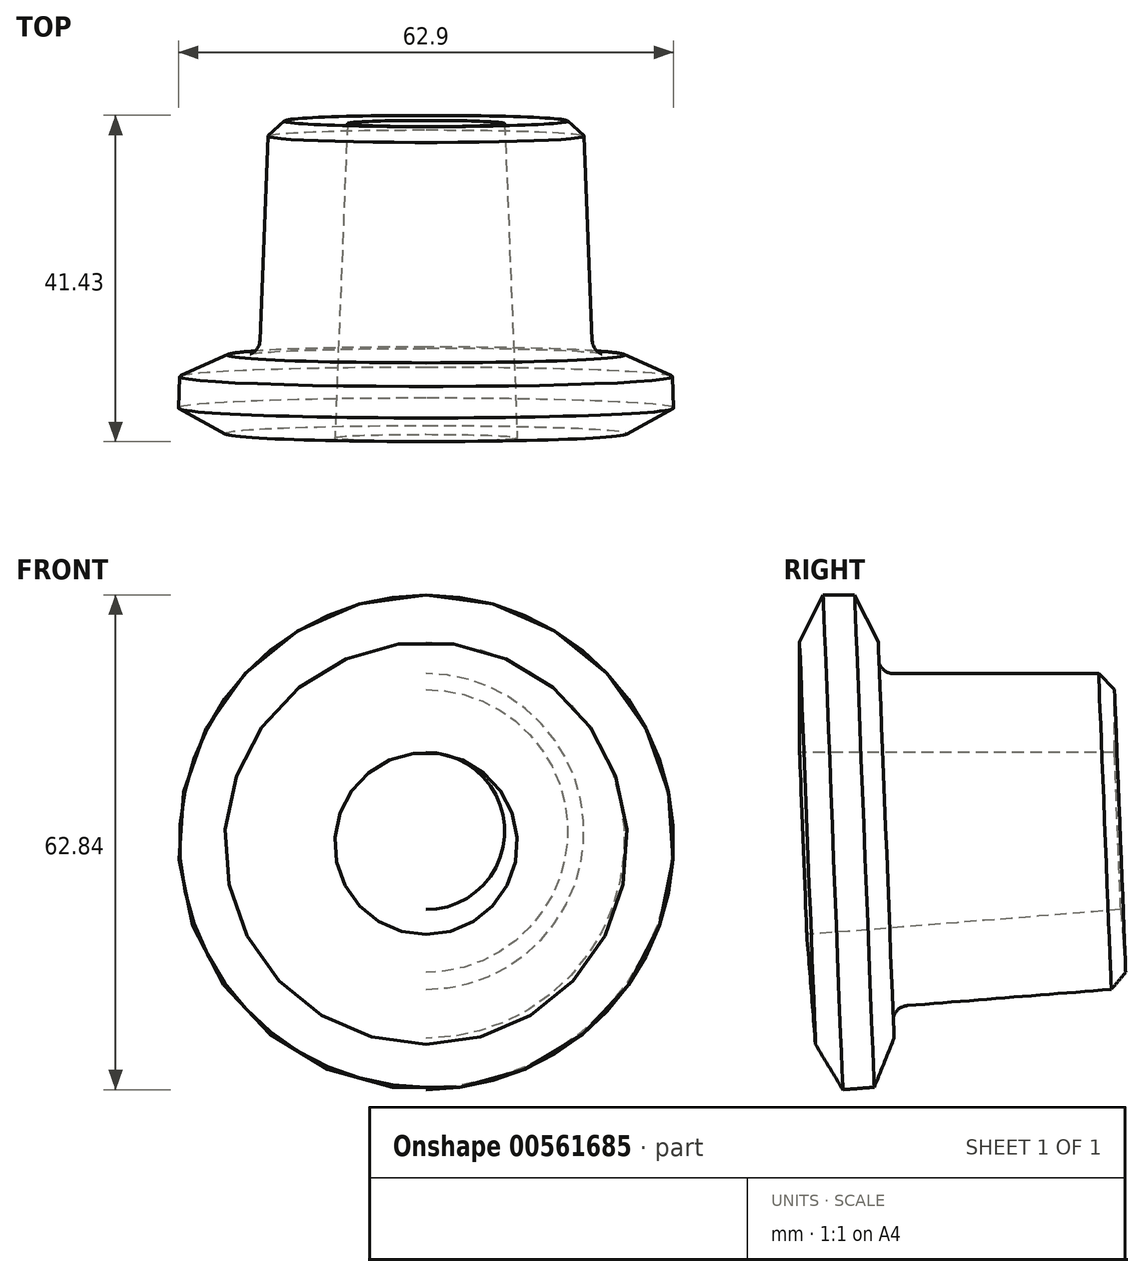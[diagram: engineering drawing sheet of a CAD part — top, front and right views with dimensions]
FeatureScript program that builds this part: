
annotation { "Feature Type Name" : "Feature", "Feature Type Description" : "" }
export const myFeature = defineFeature(function(context is Context, id is Id, definition is map)
    precondition{}
    {
        {
            var Q0;
            Q0=qCreatedBy(makeId("Right.planeOp"),FACE);
            var sketch = newSketch(context, id + "F0", { "sketchPlane" : qUnion([Q0])});
            skLineSegment(sketch, "E0.top", {"start": v(27.86, 32.7) * mm, "end": v(37.86, 32.7) * mm});
            skLineSegment(sketch, "E1.top", {"start": v(27.86, 22.7) * mm, "end": v(67.86, 22.7) * mm});
            skLineSegment(sketch, "E1.right", {"start": v(67.86, 12.7) * mm, "end": v(67.86, 22.7) * mm});
            skLineSegment(sketch, "E2.MirrorCS", {"start": v(27.86, 12.7) * mm, "end": v(31.57, 12.7) * mm});
            skLineSegment(sketch, "E3.MirrorCS", {"start": v(37.86, 12.7) * mm, "end": v(67.86, 12.7) * mm});
            skLineSegment(sketch, "E4", {"start": v(31.57, 12.7) * mm, "end": v(37.86, 12.7) * mm});
            skLineSegment(sketch, "E5", {"start": v(27.86, 12.7) * mm, "end": v(27.86, 22.7) * mm});
            skLineSegment(sketch, "E6", {"start": v(37.86, 12.7) * mm, "end": v(37.86, 32.7) * mm});
            skLineSegment(sketch, "E7.trimOffspring", {"start": v(27.86, 12.7) * mm, "end": v(27.86, 32.7) * mm});
            skLineSegment(sketch, "E8", {"start": v(27.86, 12.7) * mm, "end": v(27.86, -7.3) * mm, "construction": true});
            skLineSegment(sketch, "E9", {"start": v(37.86, 12.7) * mm, "end": v(37.86, -7.3) * mm, "construction": true});
            skLineSegment(sketch, "E10", {"start": v(67.86, 12.7) * mm, "end": v(67.86, -7.3) * mm, "construction": true});
            skLineSegment(sketch, "E11", {"start": v(0, 0) * mm, "end": v(67.86, 2.7) * mm, "construction": true});
            skSolve(sketch);
        }
        {
            var Q0;
            {var subQ6=sQuery(id+"F0.wireOp",EDGE,"E2.MirrorCS");Q0=makeQuery(id+"F0.imprint","IMPRINT",FACE,{"disambiguationData":[TD([[makeQuery(id+"F0.imprint","IMPRINT",EDGE,{"derivedFrom":subQ6}),1.0]])]});}
            var Q1;
            {var subQ0=sQuery(id+"F0.wireOp",EDGE,"E1.right");Q1=makeQuery(id+"F0.imprint","IMPRINT",FACE,{"disambiguationData":[TD([[makeQuery(id+"F0.imprint","IMPRINT",EDGE,{"derivedFrom":subQ0}),1.0]])]});}
            var Q2;
            {var subQ0=sQuery(id+"F0.wireOp",EDGE,"E0.top");Q2=makeQuery(id+"F0.imprint","IMPRINT",FACE,{"disambiguationData":[TD([[makeQuery(id+"F0.imprint","IMPRINT",EDGE,{"derivedFrom":subQ0}),-1.0]])]});}
            var Q3;
            Q3=sQuery(id+"F0.wireOp",EDGE,"E11");
            revolve(context, id + "F1", {"entities" : qUnion([Q0, Q1, Q2]), "axis" : qUnion([Q3]), "revolveType" : RevolveType.FULL});
        }
        {
            var Q0;
            Q0=makeQuery(id+"F1.opRevolve","SWEPT_EDGE",EDGE,{"disambiguationData":[OSD([sQuery(id+"F0.wireOp",EDGE,"E1.top"),sQuery(id+"F0.wireOp",EDGE,"E6")])]});
            fillet(context, id + "F2", {"entities" : qUnion([Q0]), "radius" : 2 * mm, "tangentPropagation" : true, "allowEdgeOverflow" : false});
        }
        {
            var Q0;
            Q0=makeQuery(id+"F1.opRevolve","SWEPT_EDGE",EDGE,{"disambiguationData":[OSD([sQuery(id+"F0.wireOp",EDGE,"E1.top"),sQuery(id+"F0.wireOp",EDGE,"E1.right")])]});
            chamfer(context, id + "F3", {"entities" : qUnion([Q0]), "width" : 2 * mm, "tangentPropagation" : true});
        }
        {
            var Q0;
            Q0=makeQuery(id+"F1.opRevolve","SWEPT_EDGE",EDGE,{"disambiguationData":[OSD([sQuery(id+"F0.wireOp",EDGE,"E0.top"),sQuery(id+"F0.wireOp",EDGE,"E6")])]});
            var Q1;
            Q1=makeQuery(id+"F1.opRevolve","SWEPT_EDGE",EDGE,{"disambiguationData":[OSD([sQuery(id+"F0.wireOp",EDGE,"E0.top"),sQuery(id+"F0.wireOp",EDGE,"E7.trimOffspring")])]});
            chamfer(context, id + "F4", {"entities" : qUnion([Q0, Q1]), "chamferType" : ChamferType.TWO_OFFSETS, "width1" : 3 * mm, "oppositeDirection" : false, "width2" : 6 * mm, "tangentPropagation" : true});
        }
    });
